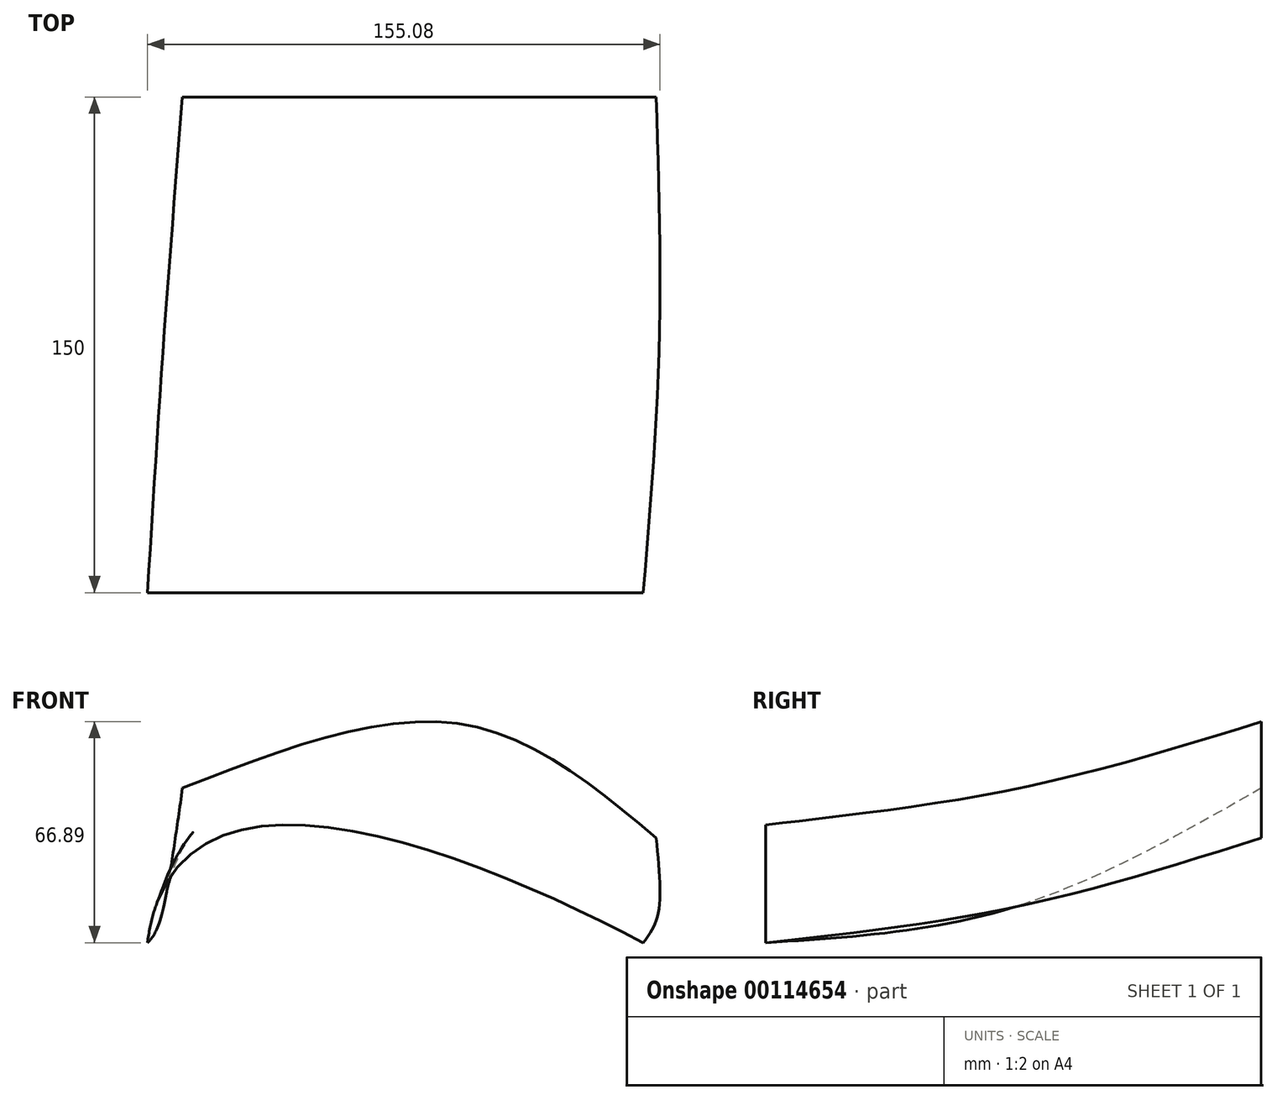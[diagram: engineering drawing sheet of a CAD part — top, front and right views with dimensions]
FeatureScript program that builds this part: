
annotation { "Feature Type Name" : "Feature", "Feature Type Description" : "" }
export const myFeature = defineFeature(function(context is Context, id is Id, definition is map)
    precondition{}
    {
        {
            var Q0;
            Q0=qCreatedBy(makeId("Front.planeOp"),FACE);
            cPlane(context, id + "F0", {"entities" : qUnion([Q0]), "cplaneType" : CPlaneType.OFFSET, "offset" : 75 * mm, "oppositeDirection" : true, "width" : 150 * mm, "height" : 150 * mm});
        }
        {
            var Q0;
            Q0=qCreatedBy(makeId("Front.planeOp"),FACE);
            cPlane(context, id + "F1", {"entities" : qUnion([Q0]), "cplaneType" : CPlaneType.OFFSET, "offset" : 75 * mm, "width" : 150 * mm, "height" : 150 * mm});
        }
        {
            var Q0;
            Q0=qCreatedBy(makeId("Front.planeOp"),FACE);
            var sketch = newSketch(context, id + "F2", { "sketchPlane" : qUnion([Q0])});
            skPoint(sketch, "E0", {"position": v(-75, 0) * mm});
            skPoint(sketch, "E1", {"position": v(75, 0) * mm});
            skFitSpline(sketch, "E2", {"points": [v(-75, 0) * mm, v(75, 0) * mm], "startDerivative": vector(24.8, 195.06) * mm, "endDerivative": vector(150.08, -78.99) * mm});
            skSolve(sketch);
        }
        {
            var Q0;
            Q0=qCreatedBy(id+"F1.planeOp",FACE);
            var sketch = newSketch(context, id + "F3", { "sketchPlane" : qUnion([Q0])});
            skPoint(sketch, "E3", {"position": v(-79.82, -10.74) * mm});
            skPoint(sketch, "E4", {"position": v(70.18, -10.74) * mm});
            skFitSpline(sketch, "E5", {"points": [v(-79.82, -10.74) * mm, v(70.18, -10.74) * mm], "startDerivative": vector(24.8, 195.06) * mm, "endDerivative": vector(150.08, -78.99) * mm});
            skSolve(sketch);
        }
        {
            var Q0;
            Q0=qCreatedBy(id+"F0.planeOp",FACE);
            var sketch = newSketch(context, id + "F4", { "sketchPlane" : qUnion([Q0])});
            skFitSpline(sketch, "E6", {"points": [v(-69.24, 36.04) * mm, v(14.83, 55.43) * mm, v(74.1, 20.94) * mm], "startDerivative": vector(167.8, 65.7) * mm, "endDerivative": vector(117.92, -99.05) * mm});
            skSolve(sketch);
        }
        {
            var Q0;
            Q0=sQuery(id+"F4.wireOp",EDGE,"E6");
            var Q1;
            Q1=sQuery(id+"F2.wireOp",EDGE,"E2");
            var Q2;
            Q2=sQuery(id+"F3.wireOp",EDGE,"E5");
            loft(context, id + "F5", {"bodyType" : ToolBodyType.SURFACE, "wireProfilesArray" : [{ "wireProfileEntities" : qUnion([Q0]) }, { "wireProfileEntities" : qUnion([Q1]) }, { "wireProfileEntities" : qUnion([Q2]) }]});
        }
    });
